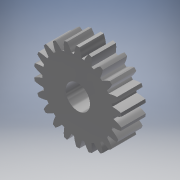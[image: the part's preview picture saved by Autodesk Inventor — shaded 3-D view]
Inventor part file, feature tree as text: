
AUTODESK INVENTOR PART (.ipt)
format: ipt  version: 2019 (Build 230136000, 136)  size: 238,592 bytes
history: native  units: mm (DEFAULTED — no unit token found)
features: plane x3, other x3, sketch x3, extrude x2
ambient origin geometry x8: Origin, YZ Plane, XZ Plane, XY Plane, X Axis, Y Axis, Z Axis, Center Point
bodies: Solid1 (feature_tree)
feature tree (11):
  extrude  "Extrusion1"  Depth=10.0mm TaperAngle=0.0deg
  plane  "Work Plane2"
  plane  "Work Plane8"
  plane  "Work Plane9"
  other  "正齒輪"
  extrude  "擠出2"  Depth=10.0mm TaperAngle=0.0deg
  sketch  "Sketch1"  dims[d0=35.980829mm d1=10.0mm d2=0.0mm]
  sketch  "Sketch2"  dims[d3=33.257759mm d4=10.0mm d5=0.0mm d16=43.083915mm d17=0.0mm d34=1.427997mm d39=0.0mm d41=0.0mm d43=43.083915mm d46=43.083915mm d47=0.0mm d48=0.0mm d49=10.0mm d50=10.0mm d51=0.0mm]
  other  "Srf1"
  sketch  "草圖3"
  other  "節圓直徑"
